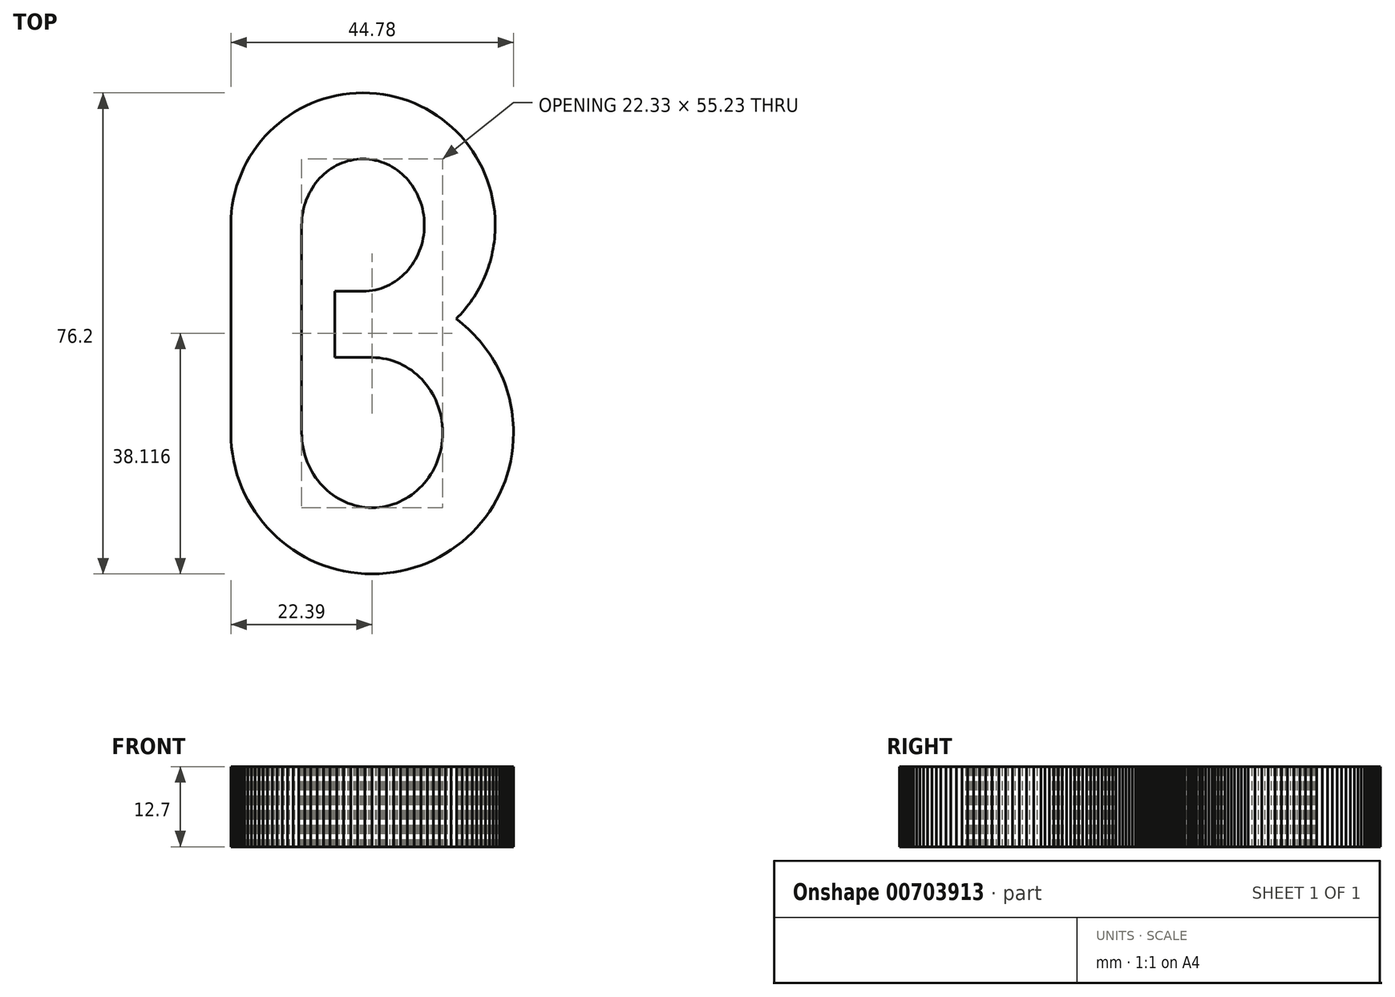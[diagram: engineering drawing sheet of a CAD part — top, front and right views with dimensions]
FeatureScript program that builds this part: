
annotation { "Feature Type Name" : "Feature", "Feature Type Description" : "" }
export const myFeature = defineFeature(function(context is Context, id is Id, definition is map)
    precondition{}
    {
        {
            var Q0;
            Q0=qCreatedBy(makeId("Top.planeOp"),FACE);
            var sketch = newSketch(context, id + "F0", { "sketchPlane" : qUnion([Q0])});
            skLineSegment(sketch, "E0", {"start": v(13.3, 2.3) * mm, "end": v(13.66, 2.66) * mm});
            skLineSegment(sketch, "E1", {"start": v(13.66, 2.66) * mm, "end": v(14, 3.03) * mm});
            skLineSegment(sketch, "E2", {"start": v(14, 3.03) * mm, "end": v(14.34, 3.4) * mm});
            skLineSegment(sketch, "E3", {"start": v(14.34, 3.4) * mm, "end": v(14.67, 3.8) * mm});
            skLineSegment(sketch, "E4", {"start": v(14.67, 3.8) * mm, "end": v(14.99, 4.18) * mm});
            skLineSegment(sketch, "E5", {"start": v(14.99, 4.18) * mm, "end": v(15.3, 4.58) * mm});
            skLineSegment(sketch, "E6", {"start": v(15.3, 4.58) * mm, "end": v(15.6, 5) * mm});
            skLineSegment(sketch, "E7", {"start": v(15.6, 5) * mm, "end": v(15.89, 5.4) * mm});
            skLineSegment(sketch, "E8", {"start": v(15.89, 5.4) * mm, "end": v(16.16, 5.83) * mm});
            skLineSegment(sketch, "E9", {"start": v(16.16, 5.83) * mm, "end": v(16.43, 6.26) * mm});
            skLineSegment(sketch, "E10", {"start": v(16.43, 6.26) * mm, "end": v(16.7, 6.7) * mm});
            skLineSegment(sketch, "E11", {"start": v(16.7, 6.7) * mm, "end": v(16.94, 7.14) * mm});
            skLineSegment(sketch, "E12", {"start": v(16.94, 7.14) * mm, "end": v(17.18, 7.59) * mm});
            skLineSegment(sketch, "E13", {"start": v(17.18, 7.59) * mm, "end": v(17.4, 8.04) * mm});
            skLineSegment(sketch, "E14", {"start": v(17.4, 8.04) * mm, "end": v(17.63, 8.5) * mm});
            skLineSegment(sketch, "E15", {"start": v(17.63, 8.5) * mm, "end": v(17.83, 8.97) * mm});
            skLineSegment(sketch, "E16", {"start": v(17.83, 8.97) * mm, "end": v(18.03, 9.45) * mm});
            skLineSegment(sketch, "E17", {"start": v(18.03, 9.45) * mm, "end": v(18.2, 9.93) * mm});
            skLineSegment(sketch, "E18", {"start": v(18.2, 9.93) * mm, "end": v(18.38, 10.41) * mm});
            skLineSegment(sketch, "E19", {"start": v(18.38, 10.41) * mm, "end": v(18.54, 10.9) * mm});
            skLineSegment(sketch, "E20", {"start": v(18.54, 10.9) * mm, "end": v(18.7, 11.4) * mm});
            skLineSegment(sketch, "E21", {"start": v(18.7, 11.4) * mm, "end": v(18.83, 11.9) * mm});
            skLineSegment(sketch, "E22", {"start": v(18.83, 11.9) * mm, "end": v(18.95, 12.4) * mm});
            skLineSegment(sketch, "E23", {"start": v(18.95, 12.4) * mm, "end": v(19.06, 12.92) * mm});
            skLineSegment(sketch, "E24", {"start": v(19.06, 12.92) * mm, "end": v(19.16, 13.44) * mm});
            skLineSegment(sketch, "E25", {"start": v(19.16, 13.44) * mm, "end": v(19.25, 13.96) * mm});
            skLineSegment(sketch, "E26", {"start": v(19.25, 13.96) * mm, "end": v(19.32, 14.48) * mm});
            skLineSegment(sketch, "E27", {"start": v(19.32, 14.48) * mm, "end": v(19.38, 15) * mm});
            skLineSegment(sketch, "E28", {"start": v(19.38, 15) * mm, "end": v(19.43, 15.54) * mm});
            skLineSegment(sketch, "E29", {"start": v(19.43, 15.54) * mm, "end": v(19.46, 16.08) * mm});
            skLineSegment(sketch, "E30", {"start": v(19.46, 16.08) * mm, "end": v(19.48, 16.61) * mm});
            skLineSegment(sketch, "E31", {"start": v(19.48, 16.61) * mm, "end": v(19.5, 17.16) * mm});
            skLineSegment(sketch, "E32", {"start": v(19.5, 17.16) * mm, "end": v(19.46, 18.24) * mm});
            skLineSegment(sketch, "E33", {"start": v(19.46, 18.24) * mm, "end": v(19.38, 19.3) * mm});
            skLineSegment(sketch, "E34", {"start": v(19.38, 19.3) * mm, "end": v(19.25, 20.35) * mm});
            skLineSegment(sketch, "E35", {"start": v(19.25, 20.35) * mm, "end": v(19.07, 21.38) * mm});
            skLineSegment(sketch, "E36", {"start": v(19.07, 21.38) * mm, "end": v(18.83, 22.4) * mm});
            skLineSegment(sketch, "E37", {"start": v(18.83, 22.4) * mm, "end": v(18.55, 23.39) * mm});
            skLineSegment(sketch, "E38", {"start": v(18.55, 23.39) * mm, "end": v(18.22, 24.36) * mm});
            skLineSegment(sketch, "E39", {"start": v(18.22, 24.36) * mm, "end": v(17.85, 25.3) * mm});
            skLineSegment(sketch, "E40", {"start": v(17.85, 25.3) * mm, "end": v(17.43, 26.24) * mm});
            skLineSegment(sketch, "E41", {"start": v(17.43, 26.24) * mm, "end": v(16.96, 27.14) * mm});
            skLineSegment(sketch, "E42", {"start": v(16.96, 27.14) * mm, "end": v(16.46, 28.02) * mm});
            skLineSegment(sketch, "E43", {"start": v(16.46, 28.02) * mm, "end": v(15.91, 28.87) * mm});
            skLineSegment(sketch, "E44", {"start": v(15.91, 28.87) * mm, "end": v(15.33, 29.69) * mm});
            skLineSegment(sketch, "E45", {"start": v(15.33, 29.69) * mm, "end": v(14.7, 30.48) * mm});
            skLineSegment(sketch, "E46", {"start": v(14.7, 30.48) * mm, "end": v(14.05, 31.24) * mm});
            skLineSegment(sketch, "E47", {"start": v(14.05, 31.24) * mm, "end": v(13.36, 31.97) * mm});
            skLineSegment(sketch, "E48", {"start": v(13.36, 31.97) * mm, "end": v(12.63, 32.66) * mm});
            skLineSegment(sketch, "E49", {"start": v(12.63, 32.66) * mm, "end": v(11.87, 33.32) * mm});
            skLineSegment(sketch, "E50", {"start": v(11.87, 33.32) * mm, "end": v(11.08, 33.94) * mm});
            skLineSegment(sketch, "E51", {"start": v(11.08, 33.94) * mm, "end": v(10.26, 34.52) * mm});
            skLineSegment(sketch, "E52", {"start": v(10.26, 34.52) * mm, "end": v(9.4, 35.07) * mm});
            skLineSegment(sketch, "E53", {"start": v(9.4, 35.07) * mm, "end": v(8.53, 35.57) * mm});
            skLineSegment(sketch, "E54", {"start": v(8.53, 35.57) * mm, "end": v(7.63, 36.03) * mm});
            skLineSegment(sketch, "E55", {"start": v(7.63, 36.03) * mm, "end": v(6.7, 36.45) * mm});
            skLineSegment(sketch, "E56", {"start": v(6.7, 36.45) * mm, "end": v(5.75, 36.83) * mm});
            skLineSegment(sketch, "E57", {"start": v(5.75, 36.83) * mm, "end": v(4.78, 37.16) * mm});
            skLineSegment(sketch, "E58", {"start": v(4.78, 37.16) * mm, "end": v(3.78, 37.44) * mm});
            skLineSegment(sketch, "E59", {"start": v(3.78, 37.44) * mm, "end": v(2.77, 37.67) * mm});
            skLineSegment(sketch, "E60", {"start": v(2.77, 37.67) * mm, "end": v(1.74, 37.86) * mm});
            skLineSegment(sketch, "E61", {"start": v(1.74, 37.86) * mm, "end": v(0.7, 38) * mm});
            skLineSegment(sketch, "E62", {"start": v(0.7, 38) * mm, "end": v(-0.37, 38.07) * mm});
            skLineSegment(sketch, "E63", {"start": v(-0.37, 38.07) * mm, "end": v(-1.45, 38.1) * mm});
            skLineSegment(sketch, "E64", {"start": v(-1.45, 38.1) * mm, "end": v(-2.53, 38.07) * mm});
            skLineSegment(sketch, "E65", {"start": v(-2.53, 38.07) * mm, "end": v(-3.6, 38) * mm});
            skLineSegment(sketch, "E66", {"start": v(-3.6, 38) * mm, "end": v(-4.64, 37.86) * mm});
            skLineSegment(sketch, "E67", {"start": v(-4.64, 37.86) * mm, "end": v(-5.67, 37.67) * mm});
            skLineSegment(sketch, "E68", {"start": v(-5.67, 37.67) * mm, "end": v(-6.68, 37.44) * mm});
            skLineSegment(sketch, "E69", {"start": v(-6.68, 37.44) * mm, "end": v(-7.68, 37.16) * mm});
            skLineSegment(sketch, "E70", {"start": v(-7.68, 37.16) * mm, "end": v(-8.65, 36.83) * mm});
            skLineSegment(sketch, "E71", {"start": v(-8.65, 36.83) * mm, "end": v(-9.6, 36.45) * mm});
            skLineSegment(sketch, "E72", {"start": v(-9.6, 36.45) * mm, "end": v(-10.53, 36.03) * mm});
            skLineSegment(sketch, "E73", {"start": v(-10.53, 36.03) * mm, "end": v(-11.43, 35.57) * mm});
            skLineSegment(sketch, "E74", {"start": v(-11.43, 35.57) * mm, "end": v(-12.31, 35.07) * mm});
            skLineSegment(sketch, "E75", {"start": v(-12.31, 35.07) * mm, "end": v(-13.16, 34.52) * mm});
            skLineSegment(sketch, "E76", {"start": v(-13.16, 34.52) * mm, "end": v(-13.98, 33.94) * mm});
            skLineSegment(sketch, "E77", {"start": v(-13.98, 33.94) * mm, "end": v(-14.77, 33.32) * mm});
            skLineSegment(sketch, "E78", {"start": v(-14.77, 33.32) * mm, "end": v(-15.53, 32.66) * mm});
            skLineSegment(sketch, "E79", {"start": v(-15.53, 32.66) * mm, "end": v(-16.26, 31.97) * mm});
            skLineSegment(sketch, "E80", {"start": v(-16.26, 31.97) * mm, "end": v(-16.95, 31.24) * mm});
            skLineSegment(sketch, "E81", {"start": v(-16.95, 31.24) * mm, "end": v(-17.61, 30.48) * mm});
            skLineSegment(sketch, "E82", {"start": v(-17.61, 30.48) * mm, "end": v(-18.23, 29.69) * mm});
            skLineSegment(sketch, "E83", {"start": v(-18.23, 29.69) * mm, "end": v(-18.82, 28.87) * mm});
            skLineSegment(sketch, "E84", {"start": v(-18.82, 28.87) * mm, "end": v(-19.36, 28.02) * mm});
            skLineSegment(sketch, "E85", {"start": v(-19.36, 28.02) * mm, "end": v(-19.87, 27.14) * mm});
            skLineSegment(sketch, "E86", {"start": v(-19.87, 27.14) * mm, "end": v(-20.33, 26.24) * mm});
            skLineSegment(sketch, "E87", {"start": v(-20.33, 26.24) * mm, "end": v(-20.75, 25.3) * mm});
            skLineSegment(sketch, "E88", {"start": v(-20.75, 25.3) * mm, "end": v(-21.12, 24.36) * mm});
            skLineSegment(sketch, "E89", {"start": v(-21.12, 24.36) * mm, "end": v(-21.45, 23.39) * mm});
            skLineSegment(sketch, "E90", {"start": v(-21.45, 23.39) * mm, "end": v(-21.73, 22.4) * mm});
            skLineSegment(sketch, "E91", {"start": v(-21.73, 22.4) * mm, "end": v(-21.97, 21.38) * mm});
            skLineSegment(sketch, "E92", {"start": v(-21.97, 21.38) * mm, "end": v(-22.15, 20.35) * mm});
            skLineSegment(sketch, "E93", {"start": v(-22.15, 20.35) * mm, "end": v(-22.29, 19.3) * mm});
            skLineSegment(sketch, "E94", {"start": v(-22.29, 19.3) * mm, "end": v(-22.37, 18.24) * mm});
            skLineSegment(sketch, "E95", {"start": v(-22.37, 18.24) * mm, "end": v(-22.4, 17.16) * mm});
            skLineSegment(sketch, "E96", {"start": v(-22.4, 17.16) * mm, "end": v(-22.4, 16.51) * mm});
            skLineSegment(sketch, "E97", {"start": v(-22.4, 16.51) * mm, "end": v(-22.4, 15.8) * mm});
            skLineSegment(sketch, "E98", {"start": v(-22.4, 15.8) * mm, "end": v(-22.4, 15) * mm});
            skLineSegment(sketch, "E99", {"start": v(-22.4, 15) * mm, "end": v(-22.4, 14.16) * mm});
            skLineSegment(sketch, "E100", {"start": v(-22.4, 14.16) * mm, "end": v(-22.4, 13.25) * mm});
            skLineSegment(sketch, "E101", {"start": v(-22.4, 13.25) * mm, "end": v(-22.4, 12.3) * mm});
            skLineSegment(sketch, "E102", {"start": v(-22.4, 12.3) * mm, "end": v(-22.4, 11.28) * mm});
            skLineSegment(sketch, "E103", {"start": v(-22.4, 11.28) * mm, "end": v(-22.4, 10.23) * mm});
            skLineSegment(sketch, "E104", {"start": v(-22.4, 10.23) * mm, "end": v(-22.4, 9.14) * mm});
            skLineSegment(sketch, "E105", {"start": v(-22.4, 9.14) * mm, "end": v(-22.4, 8.01) * mm});
            skLineSegment(sketch, "E106", {"start": v(-22.4, 8.01) * mm, "end": v(-22.4, 6.85) * mm});
            skLineSegment(sketch, "E107", {"start": v(-22.4, 6.85) * mm, "end": v(-22.4, 5.67) * mm});
            skLineSegment(sketch, "E108", {"start": v(-22.4, 5.67) * mm, "end": v(-22.4, 4.47) * mm});
            skLineSegment(sketch, "E109", {"start": v(-22.4, 4.47) * mm, "end": v(-22.4, 3.26) * mm});
            skLineSegment(sketch, "E110", {"start": v(-22.4, 3.26) * mm, "end": v(-22.4, 2.03) * mm});
            skLineSegment(sketch, "E111", {"start": v(-22.4, 2.03) * mm, "end": v(-22.4, 0.8) * mm});
            skLineSegment(sketch, "E112", {"start": v(-22.4, 0.8) * mm, "end": v(-22.4, -0.43) * mm});
            skLineSegment(sketch, "E113", {"start": v(-22.4, -0.43) * mm, "end": v(-22.4, -1.66) * mm});
            skLineSegment(sketch, "E114", {"start": v(-22.4, -1.66) * mm, "end": v(-22.4, -2.88) * mm});
            skLineSegment(sketch, "E115", {"start": v(-22.4, -2.88) * mm, "end": v(-22.4, -4.08) * mm});
            skLineSegment(sketch, "E116", {"start": v(-22.4, -4.08) * mm, "end": v(-22.4, -5.27) * mm});
            skLineSegment(sketch, "E117", {"start": v(-22.4, -5.27) * mm, "end": v(-22.4, -6.43) * mm});
            skLineSegment(sketch, "E118", {"start": v(-22.4, -6.43) * mm, "end": v(-22.4, -7.57) * mm});
            skLineSegment(sketch, "E119", {"start": v(-22.4, -7.57) * mm, "end": v(-22.4, -8.67) * mm});
            skLineSegment(sketch, "E120", {"start": v(-22.4, -8.67) * mm, "end": v(-22.4, -9.73) * mm});
            skLineSegment(sketch, "E121", {"start": v(-22.4, -9.73) * mm, "end": v(-22.4, -10.75) * mm});
            skLineSegment(sketch, "E122", {"start": v(-22.4, -10.75) * mm, "end": v(-22.4, -11.72) * mm});
            skLineSegment(sketch, "E123", {"start": v(-22.4, -11.72) * mm, "end": v(-22.4, -12.64) * mm});
            skLineSegment(sketch, "E124", {"start": v(-22.4, -12.64) * mm, "end": v(-22.4, -13.5) * mm});
            skLineSegment(sketch, "E125", {"start": v(-22.4, -13.5) * mm, "end": v(-22.4, -14.3) * mm});
            skLineSegment(sketch, "E126", {"start": v(-22.4, -14.3) * mm, "end": v(-22.4, -15.04) * mm});
            skLineSegment(sketch, "E127", {"start": v(-22.4, -15.04) * mm, "end": v(-22.4, -15.7) * mm});
            skLineSegment(sketch, "E128", {"start": v(-22.4, -15.7) * mm, "end": v(-22.36, -16.86) * mm});
            skLineSegment(sketch, "E129", {"start": v(-22.36, -16.86) * mm, "end": v(-22.28, -18) * mm});
            skLineSegment(sketch, "E130", {"start": v(-22.28, -18) * mm, "end": v(-22.14, -19.12) * mm});
            skLineSegment(sketch, "E131", {"start": v(-22.14, -19.12) * mm, "end": v(-21.94, -20.22) * mm});
            skLineSegment(sketch, "E132", {"start": v(-21.94, -20.22) * mm, "end": v(-21.69, -21.3) * mm});
            skLineSegment(sketch, "E133", {"start": v(-21.69, -21.3) * mm, "end": v(-21.39, -22.37) * mm});
            skLineSegment(sketch, "E134", {"start": v(-21.39, -22.37) * mm, "end": v(-21.03, -23.4) * mm});
            skLineSegment(sketch, "E135", {"start": v(-21.03, -23.4) * mm, "end": v(-20.63, -24.42) * mm});
            skLineSegment(sketch, "E136", {"start": v(-20.63, -24.42) * mm, "end": v(-20.18, -25.42) * mm});
            skLineSegment(sketch, "E137", {"start": v(-20.18, -25.42) * mm, "end": v(-19.7, -26.38) * mm});
            skLineSegment(sketch, "E138", {"start": v(-19.7, -26.38) * mm, "end": v(-19.15, -27.32) * mm});
            skLineSegment(sketch, "E139", {"start": v(-19.15, -27.32) * mm, "end": v(-18.57, -28.23) * mm});
            skLineSegment(sketch, "E140", {"start": v(-18.57, -28.23) * mm, "end": v(-17.94, -29.1) * mm});
            skLineSegment(sketch, "E141", {"start": v(-17.94, -29.1) * mm, "end": v(-17.28, -29.95) * mm});
            skLineSegment(sketch, "E142", {"start": v(-17.28, -29.95) * mm, "end": v(-16.58, -30.76) * mm});
            skLineSegment(sketch, "E143", {"start": v(-16.58, -30.76) * mm, "end": v(-15.83, -31.54) * mm});
            skLineSegment(sketch, "E144", {"start": v(-15.83, -31.54) * mm, "end": v(-15.06, -32.28) * mm});
            skLineSegment(sketch, "E145", {"start": v(-15.06, -32.28) * mm, "end": v(-14.24, -32.99) * mm});
            skLineSegment(sketch, "E146", {"start": v(-14.24, -32.99) * mm, "end": v(-13.4, -33.65) * mm});
            skLineSegment(sketch, "E147", {"start": v(-13.4, -33.65) * mm, "end": v(-12.52, -34.28) * mm});
            skLineSegment(sketch, "E148", {"start": v(-12.52, -34.28) * mm, "end": v(-11.61, -34.86) * mm});
            skLineSegment(sketch, "E149", {"start": v(-11.61, -34.86) * mm, "end": v(-10.67, -35.4) * mm});
            skLineSegment(sketch, "E150", {"start": v(-10.67, -35.4) * mm, "end": v(-9.7, -35.9) * mm});
            skLineSegment(sketch, "E151", {"start": v(-9.7, -35.9) * mm, "end": v(-8.72, -36.34) * mm});
            skLineSegment(sketch, "E152", {"start": v(-8.72, -36.34) * mm, "end": v(-7.7, -36.74) * mm});
            skLineSegment(sketch, "E153", {"start": v(-7.7, -36.74) * mm, "end": v(-6.66, -37.1) * mm});
            skLineSegment(sketch, "E154", {"start": v(-6.66, -37.1) * mm, "end": v(-5.6, -37.4) * mm});
            skLineSegment(sketch, "E155", {"start": v(-5.6, -37.4) * mm, "end": v(-4.51, -37.65) * mm});
            skLineSegment(sketch, "E156", {"start": v(-4.51, -37.65) * mm, "end": v(-3.41, -37.84) * mm});
            skLineSegment(sketch, "E157", {"start": v(-3.41, -37.84) * mm, "end": v(-2.29, -37.98) * mm});
            skLineSegment(sketch, "E158", {"start": v(-2.29, -37.98) * mm, "end": v(-1.15, -38.07) * mm});
            skLineSegment(sketch, "E159", {"start": v(-1.15, -38.07) * mm, "end": v(0, -38.1) * mm});
            skLineSegment(sketch, "E160", {"start": v(0, -38.1) * mm, "end": v(1.15, -38.07) * mm});
            skLineSegment(sketch, "E161", {"start": v(1.15, -38.07) * mm, "end": v(2.29, -37.98) * mm});
            skLineSegment(sketch, "E162", {"start": v(2.29, -37.98) * mm, "end": v(3.41, -37.84) * mm});
            skLineSegment(sketch, "E163", {"start": v(3.41, -37.84) * mm, "end": v(4.51, -37.65) * mm});
            skLineSegment(sketch, "E164", {"start": v(4.51, -37.65) * mm, "end": v(5.6, -37.4) * mm});
            skLineSegment(sketch, "E165", {"start": v(5.6, -37.4) * mm, "end": v(6.66, -37.1) * mm});
            skLineSegment(sketch, "E166", {"start": v(6.66, -37.1) * mm, "end": v(7.7, -36.74) * mm});
            skLineSegment(sketch, "E167", {"start": v(7.7, -36.74) * mm, "end": v(8.72, -36.34) * mm});
            skLineSegment(sketch, "E168", {"start": v(8.72, -36.34) * mm, "end": v(9.7, -35.9) * mm});
            skLineSegment(sketch, "E169", {"start": v(9.7, -35.9) * mm, "end": v(10.67, -35.4) * mm});
            skLineSegment(sketch, "E170", {"start": v(10.67, -35.4) * mm, "end": v(11.61, -34.86) * mm});
            skLineSegment(sketch, "E171", {"start": v(11.61, -34.86) * mm, "end": v(12.52, -34.28) * mm});
            skLineSegment(sketch, "E172", {"start": v(12.52, -34.28) * mm, "end": v(13.4, -33.65) * mm});
            skLineSegment(sketch, "E173", {"start": v(13.4, -33.65) * mm, "end": v(14.24, -32.99) * mm});
            skLineSegment(sketch, "E174", {"start": v(14.24, -32.99) * mm, "end": v(15.06, -32.28) * mm});
            skLineSegment(sketch, "E175", {"start": v(15.06, -32.28) * mm, "end": v(15.83, -31.54) * mm});
            skLineSegment(sketch, "E176", {"start": v(15.83, -31.54) * mm, "end": v(16.58, -30.76) * mm});
            skLineSegment(sketch, "E177", {"start": v(16.58, -30.76) * mm, "end": v(17.28, -29.95) * mm});
            skLineSegment(sketch, "E178", {"start": v(17.28, -29.95) * mm, "end": v(17.94, -29.1) * mm});
            skLineSegment(sketch, "E179", {"start": v(17.94, -29.1) * mm, "end": v(18.57, -28.23) * mm});
            skLineSegment(sketch, "E180", {"start": v(18.57, -28.23) * mm, "end": v(19.15, -27.32) * mm});
            skLineSegment(sketch, "E181", {"start": v(19.15, -27.32) * mm, "end": v(19.7, -26.38) * mm});
            skLineSegment(sketch, "E182", {"start": v(19.7, -26.38) * mm, "end": v(20.18, -25.42) * mm});
            skLineSegment(sketch, "E183", {"start": v(20.18, -25.42) * mm, "end": v(20.63, -24.42) * mm});
            skLineSegment(sketch, "E184", {"start": v(20.63, -24.42) * mm, "end": v(21.03, -23.4) * mm});
            skLineSegment(sketch, "E185", {"start": v(21.03, -23.4) * mm, "end": v(21.39, -22.37) * mm});
            skLineSegment(sketch, "E186", {"start": v(21.39, -22.37) * mm, "end": v(21.69, -21.3) * mm});
            skLineSegment(sketch, "E187", {"start": v(21.69, -21.3) * mm, "end": v(21.94, -20.22) * mm});
            skLineSegment(sketch, "E188", {"start": v(21.94, -20.22) * mm, "end": v(22.14, -19.12) * mm});
            skLineSegment(sketch, "E189", {"start": v(22.14, -19.12) * mm, "end": v(22.28, -18) * mm});
            skLineSegment(sketch, "E190", {"start": v(22.28, -18) * mm, "end": v(22.36, -16.86) * mm});
            skLineSegment(sketch, "E191", {"start": v(22.36, -16.86) * mm, "end": v(22.4, -15.7) * mm});
            skLineSegment(sketch, "E192", {"start": v(22.4, -15.7) * mm, "end": v(22.38, -15.02) * mm});
            skLineSegment(sketch, "E193", {"start": v(22.38, -15.02) * mm, "end": v(22.35, -14.33) * mm});
            skLineSegment(sketch, "E194", {"start": v(22.35, -14.33) * mm, "end": v(22.3, -13.65) * mm});
            skLineSegment(sketch, "E195", {"start": v(22.3, -13.65) * mm, "end": v(22.23, -12.98) * mm});
            skLineSegment(sketch, "E196", {"start": v(22.23, -12.98) * mm, "end": v(22.14, -12.31) * mm});
            skLineSegment(sketch, "E197", {"start": v(22.14, -12.31) * mm, "end": v(22.03, -11.65) * mm});
            skLineSegment(sketch, "E198", {"start": v(22.03, -11.65) * mm, "end": v(21.9, -11) * mm});
            skLineSegment(sketch, "E199", {"start": v(21.9, -11) * mm, "end": v(21.75, -10.35) * mm});
            skLineSegment(sketch, "E200", {"start": v(21.75, -10.35) * mm, "end": v(21.58, -9.71) * mm});
            skLineSegment(sketch, "E201", {"start": v(21.58, -9.71) * mm, "end": v(21.4, -9.08) * mm});
            skLineSegment(sketch, "E202", {"start": v(21.4, -9.08) * mm, "end": v(21.2, -8.46) * mm});
            skLineSegment(sketch, "E203", {"start": v(21.2, -8.46) * mm, "end": v(20.97, -7.84) * mm});
            skLineSegment(sketch, "E204", {"start": v(20.97, -7.84) * mm, "end": v(20.73, -7.23) * mm});
            skLineSegment(sketch, "E205", {"start": v(20.73, -7.23) * mm, "end": v(20.48, -6.63) * mm});
            skLineSegment(sketch, "E206", {"start": v(20.48, -6.63) * mm, "end": v(20.2, -6.04) * mm});
            skLineSegment(sketch, "E207", {"start": v(20.2, -6.04) * mm, "end": v(19.92, -5.46) * mm});
            skLineSegment(sketch, "E208", {"start": v(19.92, -5.46) * mm, "end": v(19.61, -4.9) * mm});
            skLineSegment(sketch, "E209", {"start": v(19.61, -4.9) * mm, "end": v(19.3, -4.33) * mm});
            skLineSegment(sketch, "E210", {"start": v(19.3, -4.33) * mm, "end": v(18.96, -3.78) * mm});
            skLineSegment(sketch, "E211", {"start": v(18.96, -3.78) * mm, "end": v(18.6, -3.24) * mm});
            skLineSegment(sketch, "E212", {"start": v(18.6, -3.24) * mm, "end": v(18.24, -2.71) * mm});
            skLineSegment(sketch, "E213", {"start": v(18.24, -2.71) * mm, "end": v(17.86, -2.2) * mm});
            skLineSegment(sketch, "E214", {"start": v(17.86, -2.2) * mm, "end": v(17.46, -1.69) * mm});
            skLineSegment(sketch, "E215", {"start": v(17.46, -1.69) * mm, "end": v(17.05, -1.2) * mm});
            skLineSegment(sketch, "E216", {"start": v(17.05, -1.2) * mm, "end": v(16.63, -0.71) * mm});
            skLineSegment(sketch, "E217", {"start": v(16.63, -0.71) * mm, "end": v(16.2, -0.24) * mm});
            skLineSegment(sketch, "E218", {"start": v(16.2, -0.24) * mm, "end": v(15.74, 0.22) * mm});
            skLineSegment(sketch, "E219", {"start": v(15.74, 0.22) * mm, "end": v(15.28, 0.66) * mm});
            skLineSegment(sketch, "E220", {"start": v(15.28, 0.66) * mm, "end": v(14.8, 1.1) * mm});
            skLineSegment(sketch, "E221", {"start": v(14.8, 1.1) * mm, "end": v(14.32, 1.5) * mm});
            skLineSegment(sketch, "E222", {"start": v(14.32, 1.5) * mm, "end": v(13.82, 1.91) * mm});
            skLineSegment(sketch, "E223", {"start": v(13.82, 1.91) * mm, "end": v(13.3, 2.3) * mm});
            skLineSegment(sketch, "E224", {"start": v(0, -27.6) * mm, "end": v(-0.57, -27.58) * mm});
            skLineSegment(sketch, "E225", {"start": v(-0.57, -27.58) * mm, "end": v(-1.14, -27.54) * mm});
            skLineSegment(sketch, "E226", {"start": v(-1.14, -27.54) * mm, "end": v(-1.7, -27.46) * mm});
            skLineSegment(sketch, "E227", {"start": v(-1.7, -27.46) * mm, "end": v(-2.25, -27.36) * mm});
            skLineSegment(sketch, "E228", {"start": v(-2.25, -27.36) * mm, "end": v(-2.8, -27.22) * mm});
            skLineSegment(sketch, "E229", {"start": v(-2.8, -27.22) * mm, "end": v(-3.32, -27.06) * mm});
            skLineSegment(sketch, "E230", {"start": v(-3.32, -27.06) * mm, "end": v(-3.84, -26.88) * mm});
            skLineSegment(sketch, "E231", {"start": v(-3.84, -26.88) * mm, "end": v(-4.35, -26.66) * mm});
            skLineSegment(sketch, "E232", {"start": v(-4.35, -26.66) * mm, "end": v(-4.84, -26.42) * mm});
            skLineSegment(sketch, "E233", {"start": v(-4.84, -26.42) * mm, "end": v(-5.32, -26.16) * mm});
            skLineSegment(sketch, "E234", {"start": v(-5.32, -26.16) * mm, "end": v(-5.79, -25.88) * mm});
            skLineSegment(sketch, "E235", {"start": v(-5.79, -25.88) * mm, "end": v(-6.24, -25.57) * mm});
            skLineSegment(sketch, "E236", {"start": v(-6.24, -25.57) * mm, "end": v(-6.68, -25.24) * mm});
            skLineSegment(sketch, "E237", {"start": v(-6.68, -25.24) * mm, "end": v(-7.1, -24.88) * mm});
            skLineSegment(sketch, "E238", {"start": v(-7.1, -24.88) * mm, "end": v(-7.5, -24.5) * mm});
            skLineSegment(sketch, "E239", {"start": v(-7.5, -24.5) * mm, "end": v(-7.9, -24.11) * mm});
            skLineSegment(sketch, "E240", {"start": v(-7.9, -24.11) * mm, "end": v(-8.26, -23.7) * mm});
            skLineSegment(sketch, "E241", {"start": v(-8.26, -23.7) * mm, "end": v(-8.62, -23.27) * mm});
            skLineSegment(sketch, "E242", {"start": v(-8.62, -23.27) * mm, "end": v(-8.95, -22.82) * mm});
            skLineSegment(sketch, "E243", {"start": v(-8.95, -22.82) * mm, "end": v(-9.26, -22.35) * mm});
            skLineSegment(sketch, "E244", {"start": v(-9.26, -22.35) * mm, "end": v(-9.55, -21.87) * mm});
            skLineSegment(sketch, "E245", {"start": v(-9.55, -21.87) * mm, "end": v(-9.82, -21.37) * mm});
            skLineSegment(sketch, "E246", {"start": v(-9.82, -21.37) * mm, "end": v(-10.06, -20.86) * mm});
            skLineSegment(sketch, "E247", {"start": v(-10.06, -20.86) * mm, "end": v(-10.29, -20.34) * mm});
            skLineSegment(sketch, "E248", {"start": v(-10.29, -20.34) * mm, "end": v(-10.49, -19.8) * mm});
            skLineSegment(sketch, "E249", {"start": v(-10.49, -19.8) * mm, "end": v(-10.66, -19.24) * mm});
            skLineSegment(sketch, "E250", {"start": v(-10.66, -19.24) * mm, "end": v(-10.81, -18.68) * mm});
            skLineSegment(sketch, "E251", {"start": v(-10.81, -18.68) * mm, "end": v(-10.94, -18.1) * mm});
            skLineSegment(sketch, "E252", {"start": v(-10.94, -18.1) * mm, "end": v(-11.04, -17.52) * mm});
            skLineSegment(sketch, "E253", {"start": v(-11.04, -17.52) * mm, "end": v(-11.1, -16.92) * mm});
            skLineSegment(sketch, "E254", {"start": v(-11.1, -16.92) * mm, "end": v(-11.15, -16.32) * mm});
            skLineSegment(sketch, "E255", {"start": v(-11.15, -16.32) * mm, "end": v(-11.17, -15.7) * mm});
            skLineSegment(sketch, "E256", {"start": v(-11.17, -15.7) * mm, "end": v(-11.17, -15.42) * mm});
            skLineSegment(sketch, "E257", {"start": v(-11.17, -15.42) * mm, "end": v(-11.17, -14.99) * mm});
            skLineSegment(sketch, "E258", {"start": v(-11.17, -14.99) * mm, "end": v(-11.17, -14.43) * mm});
            skLineSegment(sketch, "E259", {"start": v(-11.17, -14.43) * mm, "end": v(-11.17, -13.75) * mm});
            skLineSegment(sketch, "E260", {"start": v(-11.17, -13.75) * mm, "end": v(-11.17, -12.95) * mm});
            skLineSegment(sketch, "E261", {"start": v(-11.17, -12.95) * mm, "end": v(-11.17, -12.05) * mm});
            skLineSegment(sketch, "E262", {"start": v(-11.17, -12.05) * mm, "end": v(-11.17, -11.06) * mm});
            skLineSegment(sketch, "E263", {"start": v(-11.17, -11.06) * mm, "end": v(-11.17, -9.99) * mm});
            skLineSegment(sketch, "E264", {"start": v(-11.17, -9.99) * mm, "end": v(-11.17, -8.84) * mm});
            skLineSegment(sketch, "E265", {"start": v(-11.17, -8.84) * mm, "end": v(-11.17, -7.62) * mm});
            skLineSegment(sketch, "E266", {"start": v(-11.17, -7.62) * mm, "end": v(-11.17, -6.35) * mm});
            skLineSegment(sketch, "E267", {"start": v(-11.17, -6.35) * mm, "end": v(-11.17, -5.03) * mm});
            skLineSegment(sketch, "E268", {"start": v(-11.17, -5.03) * mm, "end": v(-11.17, -3.67) * mm});
            skLineSegment(sketch, "E269", {"start": v(-11.17, -3.67) * mm, "end": v(-11.17, -2.29) * mm});
            skLineSegment(sketch, "E270", {"start": v(-11.17, -2.29) * mm, "end": v(-11.17, -0.88) * mm});
            skLineSegment(sketch, "E271", {"start": v(-11.17, -0.88) * mm, "end": v(-11.17, 0.54) * mm});
            skLineSegment(sketch, "E272", {"start": v(-11.17, 0.54) * mm, "end": v(-11.17, 1.96) * mm});
            skLineSegment(sketch, "E273", {"start": v(-11.17, 1.96) * mm, "end": v(-11.17, 3.37) * mm});
            skLineSegment(sketch, "E274", {"start": v(-11.17, 3.37) * mm, "end": v(-11.17, 4.77) * mm});
            skLineSegment(sketch, "E275", {"start": v(-11.17, 4.77) * mm, "end": v(-11.17, 6.14) * mm});
            skLineSegment(sketch, "E276", {"start": v(-11.17, 6.14) * mm, "end": v(-11.17, 7.47) * mm});
            skLineSegment(sketch, "E277", {"start": v(-11.17, 7.47) * mm, "end": v(-11.17, 8.76) * mm});
            skLineSegment(sketch, "E278", {"start": v(-11.17, 8.76) * mm, "end": v(-11.17, 10) * mm});
            skLineSegment(sketch, "E279", {"start": v(-11.17, 10) * mm, "end": v(-11.17, 11.16) * mm});
            skLineSegment(sketch, "E280", {"start": v(-11.17, 11.16) * mm, "end": v(-11.17, 12.26) * mm});
            skLineSegment(sketch, "E281", {"start": v(-11.17, 12.26) * mm, "end": v(-11.17, 13.28) * mm});
            skLineSegment(sketch, "E282", {"start": v(-11.17, 13.28) * mm, "end": v(-11.17, 14.2) * mm});
            skLineSegment(sketch, "E283", {"start": v(-11.17, 14.2) * mm, "end": v(-11.17, 15.03) * mm});
            skLineSegment(sketch, "E284", {"start": v(-11.17, 15.03) * mm, "end": v(-11.17, 15.75) * mm});
            skLineSegment(sketch, "E285", {"start": v(-11.17, 15.75) * mm, "end": v(-11.17, 16.35) * mm});
            skLineSegment(sketch, "E286", {"start": v(-11.17, 16.35) * mm, "end": v(-11.17, 16.82) * mm});
            skLineSegment(sketch, "E287", {"start": v(-11.17, 16.82) * mm, "end": v(-11.17, 17.16) * mm});
            skLineSegment(sketch, "E288", {"start": v(-11.17, 17.16) * mm, "end": v(-11.15, 17.7) * mm});
            skLineSegment(sketch, "E289", {"start": v(-11.15, 17.7) * mm, "end": v(-11.11, 18.23) * mm});
            skLineSegment(sketch, "E290", {"start": v(-11.11, 18.23) * mm, "end": v(-11.05, 18.75) * mm});
            skLineSegment(sketch, "E291", {"start": v(-11.05, 18.75) * mm, "end": v(-10.97, 19.27) * mm});
            skLineSegment(sketch, "E292", {"start": v(-10.97, 19.27) * mm, "end": v(-10.86, 19.77) * mm});
            skLineSegment(sketch, "E293", {"start": v(-10.86, 19.77) * mm, "end": v(-10.73, 20.27) * mm});
            skLineSegment(sketch, "E294", {"start": v(-10.73, 20.27) * mm, "end": v(-10.58, 20.76) * mm});
            skLineSegment(sketch, "E295", {"start": v(-10.58, 20.76) * mm, "end": v(-10.4, 21.23) * mm});
            skLineSegment(sketch, "E296", {"start": v(-10.4, 21.23) * mm, "end": v(-10.2, 21.7) * mm});
            skLineSegment(sketch, "E297", {"start": v(-10.2, 21.7) * mm, "end": v(-10, 22.15) * mm});
            skLineSegment(sketch, "E298", {"start": v(-10, 22.15) * mm, "end": v(-9.76, 22.59) * mm});
            skLineSegment(sketch, "E299", {"start": v(-9.76, 22.59) * mm, "end": v(-9.5, 23.01) * mm});
            skLineSegment(sketch, "E300", {"start": v(-9.5, 23.01) * mm, "end": v(-9.24, 23.42) * mm});
            skLineSegment(sketch, "E301", {"start": v(-9.24, 23.42) * mm, "end": v(-8.95, 23.82) * mm});
            skLineSegment(sketch, "E302", {"start": v(-8.95, 23.82) * mm, "end": v(-8.64, 24.2) * mm});
            skLineSegment(sketch, "E303", {"start": v(-8.64, 24.2) * mm, "end": v(-8.32, 24.56) * mm});
            skLineSegment(sketch, "E304", {"start": v(-8.32, 24.56) * mm, "end": v(-7.98, 24.9) * mm});
            skLineSegment(sketch, "E305", {"start": v(-7.98, 24.9) * mm, "end": v(-7.63, 25.24) * mm});
            skLineSegment(sketch, "E306", {"start": v(-7.63, 25.24) * mm, "end": v(-7.26, 25.55) * mm});
            skLineSegment(sketch, "E307", {"start": v(-7.26, 25.55) * mm, "end": v(-6.88, 25.84) * mm});
            skLineSegment(sketch, "E308", {"start": v(-6.88, 25.84) * mm, "end": v(-6.49, 26.11) * mm});
            skLineSegment(sketch, "E309", {"start": v(-6.49, 26.11) * mm, "end": v(-6.08, 26.36) * mm});
            skLineSegment(sketch, "E310", {"start": v(-6.08, 26.36) * mm, "end": v(-5.66, 26.6) * mm});
            skLineSegment(sketch, "E311", {"start": v(-5.66, 26.6) * mm, "end": v(-5.23, 26.8) * mm});
            skLineSegment(sketch, "E312", {"start": v(-5.23, 26.8) * mm, "end": v(-4.8, 27) * mm});
            skLineSegment(sketch, "E313", {"start": v(-4.8, 27) * mm, "end": v(-4.34, 27.16) * mm});
            skLineSegment(sketch, "E314", {"start": v(-4.34, 27.16) * mm, "end": v(-3.88, 27.3) * mm});
            skLineSegment(sketch, "E315", {"start": v(-3.88, 27.3) * mm, "end": v(-3.4, 27.42) * mm});
            skLineSegment(sketch, "E316", {"start": v(-3.4, 27.42) * mm, "end": v(-2.93, 27.5) * mm});
            skLineSegment(sketch, "E317", {"start": v(-2.93, 27.5) * mm, "end": v(-2.44, 27.57) * mm});
            skLineSegment(sketch, "E318", {"start": v(-2.44, 27.57) * mm, "end": v(-1.95, 27.62) * mm});
            skLineSegment(sketch, "E319", {"start": v(-1.95, 27.62) * mm, "end": v(-1.45, 27.63) * mm});
            skLineSegment(sketch, "E320", {"start": v(-1.45, 27.63) * mm, "end": v(-0.95, 27.62) * mm});
            skLineSegment(sketch, "E321", {"start": v(-0.95, 27.62) * mm, "end": v(-0.46, 27.57) * mm});
            skLineSegment(sketch, "E322", {"start": v(-0.46, 27.57) * mm, "end": v(0.03, 27.5) * mm});
            skLineSegment(sketch, "E323", {"start": v(0.03, 27.5) * mm, "end": v(0.5, 27.42) * mm});
            skLineSegment(sketch, "E324", {"start": v(0.5, 27.42) * mm, "end": v(0.98, 27.3) * mm});
            skLineSegment(sketch, "E325", {"start": v(0.98, 27.3) * mm, "end": v(1.44, 27.16) * mm});
            skLineSegment(sketch, "E326", {"start": v(1.44, 27.16) * mm, "end": v(1.89, 27) * mm});
            skLineSegment(sketch, "E327", {"start": v(1.89, 27) * mm, "end": v(2.33, 26.8) * mm});
            skLineSegment(sketch, "E328", {"start": v(2.33, 26.8) * mm, "end": v(2.76, 26.6) * mm});
            skLineSegment(sketch, "E329", {"start": v(2.76, 26.6) * mm, "end": v(3.18, 26.36) * mm});
            skLineSegment(sketch, "E330", {"start": v(3.18, 26.36) * mm, "end": v(3.59, 26.11) * mm});
            skLineSegment(sketch, "E331", {"start": v(3.59, 26.11) * mm, "end": v(3.98, 25.84) * mm});
            skLineSegment(sketch, "E332", {"start": v(3.98, 25.84) * mm, "end": v(4.36, 25.55) * mm});
            skLineSegment(sketch, "E333", {"start": v(4.36, 25.55) * mm, "end": v(4.73, 25.24) * mm});
            skLineSegment(sketch, "E334", {"start": v(4.73, 25.24) * mm, "end": v(5.08, 24.9) * mm});
            skLineSegment(sketch, "E335", {"start": v(5.08, 24.9) * mm, "end": v(5.42, 24.56) * mm});
            skLineSegment(sketch, "E336", {"start": v(5.42, 24.56) * mm, "end": v(5.74, 24.2) * mm});
            skLineSegment(sketch, "E337", {"start": v(5.74, 24.2) * mm, "end": v(6.05, 23.82) * mm});
            skLineSegment(sketch, "E338", {"start": v(6.05, 23.82) * mm, "end": v(6.33, 23.42) * mm});
            skLineSegment(sketch, "E339", {"start": v(6.33, 23.42) * mm, "end": v(6.6, 23.01) * mm});
            skLineSegment(sketch, "E340", {"start": v(6.6, 23.01) * mm, "end": v(6.86, 22.59) * mm});
            skLineSegment(sketch, "E341", {"start": v(6.86, 22.59) * mm, "end": v(7.1, 22.15) * mm});
            skLineSegment(sketch, "E342", {"start": v(7.1, 22.15) * mm, "end": v(7.3, 21.7) * mm});
            skLineSegment(sketch, "E343", {"start": v(7.3, 21.7) * mm, "end": v(7.5, 21.23) * mm});
            skLineSegment(sketch, "E344", {"start": v(7.5, 21.23) * mm, "end": v(7.67, 20.76) * mm});
            skLineSegment(sketch, "E345", {"start": v(7.67, 20.76) * mm, "end": v(7.83, 20.27) * mm});
            skLineSegment(sketch, "E346", {"start": v(7.83, 20.27) * mm, "end": v(7.96, 19.77) * mm});
            skLineSegment(sketch, "E347", {"start": v(7.96, 19.77) * mm, "end": v(8.07, 19.27) * mm});
            skLineSegment(sketch, "E348", {"start": v(8.07, 19.27) * mm, "end": v(8.15, 18.75) * mm});
            skLineSegment(sketch, "E349", {"start": v(8.15, 18.75) * mm, "end": v(8.21, 18.23) * mm});
            skLineSegment(sketch, "E350", {"start": v(8.21, 18.23) * mm, "end": v(8.25, 17.7) * mm});
            skLineSegment(sketch, "E351", {"start": v(8.25, 17.7) * mm, "end": v(8.26, 17.16) * mm});
            skLineSegment(sketch, "E352", {"start": v(8.26, 17.16) * mm, "end": v(8.25, 16.62) * mm});
            skLineSegment(sketch, "E353", {"start": v(8.25, 16.62) * mm, "end": v(8.21, 16.09) * mm});
            skLineSegment(sketch, "E354", {"start": v(8.21, 16.09) * mm, "end": v(8.15, 15.56) * mm});
            skLineSegment(sketch, "E355", {"start": v(8.15, 15.56) * mm, "end": v(8.07, 15.05) * mm});
            skLineSegment(sketch, "E356", {"start": v(8.07, 15.05) * mm, "end": v(7.96, 14.54) * mm});
            skLineSegment(sketch, "E357", {"start": v(7.96, 14.54) * mm, "end": v(7.83, 14.04) * mm});
            skLineSegment(sketch, "E358", {"start": v(7.83, 14.04) * mm, "end": v(7.67, 13.56) * mm});
            skLineSegment(sketch, "E359", {"start": v(7.67, 13.56) * mm, "end": v(7.5, 13.08) * mm});
            skLineSegment(sketch, "E360", {"start": v(7.5, 13.08) * mm, "end": v(7.3, 12.62) * mm});
            skLineSegment(sketch, "E361", {"start": v(7.3, 12.62) * mm, "end": v(7.1, 12.17) * mm});
            skLineSegment(sketch, "E362", {"start": v(7.1, 12.17) * mm, "end": v(6.86, 11.73) * mm});
            skLineSegment(sketch, "E363", {"start": v(6.86, 11.73) * mm, "end": v(6.6, 11.3) * mm});
            skLineSegment(sketch, "E364", {"start": v(6.6, 11.3) * mm, "end": v(6.33, 10.9) * mm});
            skLineSegment(sketch, "E365", {"start": v(6.33, 10.9) * mm, "end": v(6.05, 10.5) * mm});
            skLineSegment(sketch, "E366", {"start": v(6.05, 10.5) * mm, "end": v(5.74, 10.12) * mm});
            skLineSegment(sketch, "E367", {"start": v(5.74, 10.12) * mm, "end": v(5.42, 9.75) * mm});
            skLineSegment(sketch, "E368", {"start": v(5.42, 9.75) * mm, "end": v(5.08, 9.4) * mm});
            skLineSegment(sketch, "E369", {"start": v(5.08, 9.4) * mm, "end": v(4.73, 9.08) * mm});
            skLineSegment(sketch, "E370", {"start": v(4.73, 9.08) * mm, "end": v(4.36, 8.77) * mm});
            skLineSegment(sketch, "E371", {"start": v(4.36, 8.77) * mm, "end": v(3.98, 8.47) * mm});
            skLineSegment(sketch, "E372", {"start": v(3.98, 8.47) * mm, "end": v(3.59, 8.2) * mm});
            skLineSegment(sketch, "E373", {"start": v(3.59, 8.2) * mm, "end": v(3.18, 7.95) * mm});
            skLineSegment(sketch, "E374", {"start": v(3.18, 7.95) * mm, "end": v(2.76, 7.72) * mm});
            skLineSegment(sketch, "E375", {"start": v(2.76, 7.72) * mm, "end": v(2.33, 7.5) * mm});
            skLineSegment(sketch, "E376", {"start": v(2.33, 7.5) * mm, "end": v(1.89, 7.32) * mm});
            skLineSegment(sketch, "E377", {"start": v(1.89, 7.32) * mm, "end": v(1.44, 7.16) * mm});
            skLineSegment(sketch, "E378", {"start": v(1.44, 7.16) * mm, "end": v(0.98, 7.02) * mm});
            skLineSegment(sketch, "E379", {"start": v(0.98, 7.02) * mm, "end": v(0.5, 6.9) * mm});
            skLineSegment(sketch, "E380", {"start": v(0.5, 6.9) * mm, "end": v(0.03, 6.8) * mm});
            skLineSegment(sketch, "E381", {"start": v(0.03, 6.8) * mm, "end": v(-0.46, 6.74) * mm});
            skLineSegment(sketch, "E382", {"start": v(-0.46, 6.74) * mm, "end": v(-0.95, 6.7) * mm});
            skLineSegment(sketch, "E383", {"start": v(-0.95, 6.7) * mm, "end": v(-1.45, 6.69) * mm});
            skLineSegment(sketch, "E384", {"start": v(-1.45, 6.69) * mm, "end": v(-1.5, 6.69) * mm});
            skLineSegment(sketch, "E385", {"start": v(-1.5, 6.69) * mm, "end": v(-1.56, 6.69) * mm});
            skLineSegment(sketch, "E386", {"start": v(-1.56, 6.69) * mm, "end": v(-1.65, 6.69) * mm});
            skLineSegment(sketch, "E387", {"start": v(-1.65, 6.69) * mm, "end": v(-1.75, 6.69) * mm});
            skLineSegment(sketch, "E388", {"start": v(-1.75, 6.69) * mm, "end": v(-1.87, 6.69) * mm});
            skLineSegment(sketch, "E389", {"start": v(-1.87, 6.69) * mm, "end": v(-2, 6.69) * mm});
            skLineSegment(sketch, "E390", {"start": v(-2, 6.69) * mm, "end": v(-2.15, 6.69) * mm});
            skLineSegment(sketch, "E391", {"start": v(-2.15, 6.69) * mm, "end": v(-2.3, 6.69) * mm});
            skLineSegment(sketch, "E392", {"start": v(-2.3, 6.69) * mm, "end": v(-2.47, 6.69) * mm});
            skLineSegment(sketch, "E393", {"start": v(-2.47, 6.69) * mm, "end": v(-2.65, 6.69) * mm});
            skLineSegment(sketch, "E394", {"start": v(-2.65, 6.69) * mm, "end": v(-2.83, 6.69) * mm});
            skLineSegment(sketch, "E395", {"start": v(-2.83, 6.69) * mm, "end": v(-3.02, 6.69) * mm});
            skLineSegment(sketch, "E396", {"start": v(-3.02, 6.69) * mm, "end": v(-3.22, 6.69) * mm});
            skLineSegment(sketch, "E397", {"start": v(-3.22, 6.69) * mm, "end": v(-3.42, 6.69) * mm});
            skLineSegment(sketch, "E398", {"start": v(-3.42, 6.69) * mm, "end": v(-3.62, 6.69) * mm});
            skLineSegment(sketch, "E399", {"start": v(-3.62, 6.69) * mm, "end": v(-3.82, 6.69) * mm});
            skLineSegment(sketch, "E400", {"start": v(-3.82, 6.69) * mm, "end": v(-4.02, 6.69) * mm});
            skLineSegment(sketch, "E401", {"start": v(-4.02, 6.69) * mm, "end": v(-4.21, 6.69) * mm});
            skLineSegment(sketch, "E402", {"start": v(-4.21, 6.69) * mm, "end": v(-4.4, 6.69) * mm});
            skLineSegment(sketch, "E403", {"start": v(-4.4, 6.69) * mm, "end": v(-4.6, 6.69) * mm});
            skLineSegment(sketch, "E404", {"start": v(-4.6, 6.69) * mm, "end": v(-4.78, 6.69) * mm});
            skLineSegment(sketch, "E405", {"start": v(-4.78, 6.69) * mm, "end": v(-4.95, 6.69) * mm});
            skLineSegment(sketch, "E406", {"start": v(-4.95, 6.69) * mm, "end": v(-5.11, 6.69) * mm});
            skLineSegment(sketch, "E407", {"start": v(-5.11, 6.69) * mm, "end": v(-5.26, 6.69) * mm});
            skLineSegment(sketch, "E408", {"start": v(-5.26, 6.69) * mm, "end": v(-5.4, 6.69) * mm});
            skLineSegment(sketch, "E409", {"start": v(-5.4, 6.69) * mm, "end": v(-5.53, 6.69) * mm});
            skLineSegment(sketch, "E410", {"start": v(-5.53, 6.69) * mm, "end": v(-5.64, 6.69) * mm});
            skLineSegment(sketch, "E411", {"start": v(-5.64, 6.69) * mm, "end": v(-5.73, 6.69) * mm});
            skLineSegment(sketch, "E412", {"start": v(-5.73, 6.69) * mm, "end": v(-5.8, 6.69) * mm});
            skLineSegment(sketch, "E413", {"start": v(-5.8, 6.69) * mm, "end": v(-5.86, 6.69) * mm});
            skLineSegment(sketch, "E414", {"start": v(-5.86, 6.69) * mm, "end": v(-5.9, 6.69) * mm});
            skLineSegment(sketch, "E415", {"start": v(-5.9, 6.69) * mm, "end": v(-5.9, 6.69) * mm});
            skLineSegment(sketch, "E416", {"start": v(-5.9, 6.69) * mm, "end": v(-5.9, 6.36) * mm});
            skLineSegment(sketch, "E417", {"start": v(-5.9, 6.36) * mm, "end": v(-5.9, 6.03) * mm});
            skLineSegment(sketch, "E418", {"start": v(-5.9, 6.03) * mm, "end": v(-5.9, 5.7) * mm});
            skLineSegment(sketch, "E419", {"start": v(-5.9, 5.7) * mm, "end": v(-5.9, 5.37) * mm});
            skLineSegment(sketch, "E420", {"start": v(-5.9, 5.37) * mm, "end": v(-5.9, 5.05) * mm});
            skLineSegment(sketch, "E421", {"start": v(-5.9, 5.05) * mm, "end": v(-5.9, 4.72) * mm});
            skLineSegment(sketch, "E422", {"start": v(-5.9, 4.72) * mm, "end": v(-5.9, 4.39) * mm});
            skLineSegment(sketch, "E423", {"start": v(-5.9, 4.39) * mm, "end": v(-5.9, 4.06) * mm});
            skLineSegment(sketch, "E424", {"start": v(-5.9, 4.06) * mm, "end": v(-5.9, 3.73) * mm});
            skLineSegment(sketch, "E425", {"start": v(-5.9, 3.73) * mm, "end": v(-5.9, 3.4) * mm});
            skLineSegment(sketch, "E426", {"start": v(-5.9, 3.4) * mm, "end": v(-5.9, 3.08) * mm});
            skLineSegment(sketch, "E427", {"start": v(-5.9, 3.08) * mm, "end": v(-5.9, 2.75) * mm});
            skLineSegment(sketch, "E428", {"start": v(-5.9, 2.75) * mm, "end": v(-5.9, 2.42) * mm});
            skLineSegment(sketch, "E429", {"start": v(-5.9, 2.42) * mm, "end": v(-5.9, 2.1) * mm});
            skLineSegment(sketch, "E430", {"start": v(-5.9, 2.1) * mm, "end": v(-5.9, 1.76) * mm});
            skLineSegment(sketch, "E431", {"start": v(-5.9, 1.76) * mm, "end": v(-5.9, 1.44) * mm});
            skLineSegment(sketch, "E432", {"start": v(-5.9, 1.44) * mm, "end": v(-5.9, 1.1) * mm});
            skLineSegment(sketch, "E433", {"start": v(-5.9, 1.1) * mm, "end": v(-5.9, 0.78) * mm});
            skLineSegment(sketch, "E434", {"start": v(-5.9, 0.78) * mm, "end": v(-5.9, 0.45) * mm});
            skLineSegment(sketch, "E435", {"start": v(-5.9, 0.45) * mm, "end": v(-5.9, 0.12) * mm});
            skLineSegment(sketch, "E436", {"start": v(-5.9, 0.12) * mm, "end": v(-5.9, -0.2) * mm});
            skLineSegment(sketch, "E437", {"start": v(-5.9, -0.2) * mm, "end": v(-5.9, -0.53) * mm});
            skLineSegment(sketch, "E438", {"start": v(-5.9, -0.53) * mm, "end": v(-5.9, -0.86) * mm});
            skLineSegment(sketch, "E439", {"start": v(-5.9, -0.86) * mm, "end": v(-5.9, -1.2) * mm});
            skLineSegment(sketch, "E440", {"start": v(-5.9, -1.2) * mm, "end": v(-5.9, -1.52) * mm});
            skLineSegment(sketch, "E441", {"start": v(-5.9, -1.52) * mm, "end": v(-5.9, -1.85) * mm});
            skLineSegment(sketch, "E442", {"start": v(-5.9, -1.85) * mm, "end": v(-5.9, -2.18) * mm});
            skLineSegment(sketch, "E443", {"start": v(-5.9, -2.18) * mm, "end": v(-5.9, -2.5) * mm});
            skLineSegment(sketch, "E444", {"start": v(-5.9, -2.5) * mm, "end": v(-5.9, -2.83) * mm});
            skLineSegment(sketch, "E445", {"start": v(-5.9, -2.83) * mm, "end": v(-5.9, -3.16) * mm});
            skLineSegment(sketch, "E446", {"start": v(-5.9, -3.16) * mm, "end": v(-5.9, -3.49) * mm});
            skLineSegment(sketch, "E447", {"start": v(-5.9, -3.49) * mm, "end": v(-5.9, -3.82) * mm});
            skLineSegment(sketch, "E448", {"start": v(-5.9, -3.82) * mm, "end": v(-5.9, -3.82) * mm});
            skLineSegment(sketch, "E449", {"start": v(-5.9, -3.82) * mm, "end": v(-5.85, -3.82) * mm});
            skLineSegment(sketch, "E450", {"start": v(-5.85, -3.82) * mm, "end": v(-5.78, -3.82) * mm});
            skLineSegment(sketch, "E451", {"start": v(-5.78, -3.82) * mm, "end": v(-5.7, -3.82) * mm});
            skLineSegment(sketch, "E452", {"start": v(-5.7, -3.82) * mm, "end": v(-5.57, -3.82) * mm});
            skLineSegment(sketch, "E453", {"start": v(-5.57, -3.82) * mm, "end": v(-5.44, -3.82) * mm});
            skLineSegment(sketch, "E454", {"start": v(-5.44, -3.82) * mm, "end": v(-5.28, -3.82) * mm});
            skLineSegment(sketch, "E455", {"start": v(-5.28, -3.82) * mm, "end": v(-5.1, -3.82) * mm});
            skLineSegment(sketch, "E456", {"start": v(-5.1, -3.82) * mm, "end": v(-4.92, -3.82) * mm});
            skLineSegment(sketch, "E457", {"start": v(-4.92, -3.82) * mm, "end": v(-4.71, -3.82) * mm});
            skLineSegment(sketch, "E458", {"start": v(-4.71, -3.82) * mm, "end": v(-4.5, -3.82) * mm});
            skLineSegment(sketch, "E459", {"start": v(-4.5, -3.82) * mm, "end": v(-4.27, -3.82) * mm});
            skLineSegment(sketch, "E460", {"start": v(-4.27, -3.82) * mm, "end": v(-4.03, -3.82) * mm});
            skLineSegment(sketch, "E461", {"start": v(-4.03, -3.82) * mm, "end": v(-3.79, -3.82) * mm});
            skLineSegment(sketch, "E462", {"start": v(-3.79, -3.82) * mm, "end": v(-3.54, -3.82) * mm});
            skLineSegment(sketch, "E463", {"start": v(-3.54, -3.82) * mm, "end": v(-3.28, -3.82) * mm});
            skLineSegment(sketch, "E464", {"start": v(-3.28, -3.82) * mm, "end": v(-3.03, -3.82) * mm});
            skLineSegment(sketch, "E465", {"start": v(-3.03, -3.82) * mm, "end": v(-2.77, -3.82) * mm});
            skLineSegment(sketch, "E466", {"start": v(-2.77, -3.82) * mm, "end": v(-2.5, -3.82) * mm});
            skLineSegment(sketch, "E467", {"start": v(-2.5, -3.82) * mm, "end": v(-2.25, -3.82) * mm});
            skLineSegment(sketch, "E468", {"start": v(-2.25, -3.82) * mm, "end": v(-2, -3.82) * mm});
            skLineSegment(sketch, "E469", {"start": v(-2, -3.82) * mm, "end": v(-1.76, -3.82) * mm});
            skLineSegment(sketch, "E470", {"start": v(-1.76, -3.82) * mm, "end": v(-1.52, -3.82) * mm});
            skLineSegment(sketch, "E471", {"start": v(-1.52, -3.82) * mm, "end": v(-1.3, -3.82) * mm});
            skLineSegment(sketch, "E472", {"start": v(-1.3, -3.82) * mm, "end": v(-1.08, -3.82) * mm});
            skLineSegment(sketch, "E473", {"start": v(-1.08, -3.82) * mm, "end": v(-0.87, -3.82) * mm});
            skLineSegment(sketch, "E474", {"start": v(-0.87, -3.82) * mm, "end": v(-0.68, -3.82) * mm});
            skLineSegment(sketch, "E475", {"start": v(-0.68, -3.82) * mm, "end": v(-0.5, -3.82) * mm});
            skLineSegment(sketch, "E476", {"start": v(-0.5, -3.82) * mm, "end": v(-0.35, -3.82) * mm});
            skLineSegment(sketch, "E477", {"start": v(-0.35, -3.82) * mm, "end": v(-0.21, -3.82) * mm});
            skLineSegment(sketch, "E478", {"start": v(-0.21, -3.82) * mm, "end": v(-0.1, -3.82) * mm});
            skLineSegment(sketch, "E479", {"start": v(-0.1, -3.82) * mm, "end": v(0, -3.82) * mm});
            skLineSegment(sketch, "E480", {"start": v(0, -3.82) * mm, "end": v(0.57, -3.83) * mm});
            skLineSegment(sketch, "E481", {"start": v(0.57, -3.83) * mm, "end": v(1.14, -3.88) * mm});
            skLineSegment(sketch, "E482", {"start": v(1.14, -3.88) * mm, "end": v(1.7, -3.95) * mm});
            skLineSegment(sketch, "E483", {"start": v(1.7, -3.95) * mm, "end": v(2.25, -4.06) * mm});
            skLineSegment(sketch, "E484", {"start": v(2.25, -4.06) * mm, "end": v(2.8, -4.2) * mm});
            skLineSegment(sketch, "E485", {"start": v(2.8, -4.2) * mm, "end": v(3.32, -4.35) * mm});
            skLineSegment(sketch, "E486", {"start": v(3.32, -4.35) * mm, "end": v(3.84, -4.54) * mm});
            skLineSegment(sketch, "E487", {"start": v(3.84, -4.54) * mm, "end": v(4.35, -4.75) * mm});
            skLineSegment(sketch, "E488", {"start": v(4.35, -4.75) * mm, "end": v(4.84, -4.99) * mm});
            skLineSegment(sketch, "E489", {"start": v(4.84, -4.99) * mm, "end": v(5.32, -5.25) * mm});
            skLineSegment(sketch, "E490", {"start": v(5.32, -5.25) * mm, "end": v(5.79, -5.54) * mm});
            skLineSegment(sketch, "E491", {"start": v(5.79, -5.54) * mm, "end": v(6.24, -5.85) * mm});
            skLineSegment(sketch, "E492", {"start": v(6.24, -5.85) * mm, "end": v(6.68, -6.18) * mm});
            skLineSegment(sketch, "E493", {"start": v(6.68, -6.18) * mm, "end": v(7.1, -6.53) * mm});
            skLineSegment(sketch, "E494", {"start": v(7.1, -6.53) * mm, "end": v(7.5, -6.9) * mm});
            skLineSegment(sketch, "E495", {"start": v(7.5, -6.9) * mm, "end": v(7.9, -7.3) * mm});
            skLineSegment(sketch, "E496", {"start": v(7.9, -7.3) * mm, "end": v(8.26, -7.71) * mm});
            skLineSegment(sketch, "E497", {"start": v(8.26, -7.71) * mm, "end": v(8.62, -8.14) * mm});
            skLineSegment(sketch, "E498", {"start": v(8.62, -8.14) * mm, "end": v(8.95, -8.6) * mm});
            skLineSegment(sketch, "E499", {"start": v(8.95, -8.6) * mm, "end": v(9.26, -9.06) * mm});
            skLineSegment(sketch, "E500", {"start": v(9.26, -9.06) * mm, "end": v(9.55, -9.54) * mm});
            skLineSegment(sketch, "E501", {"start": v(9.55, -9.54) * mm, "end": v(9.82, -10.04) * mm});
            skLineSegment(sketch, "E502", {"start": v(9.82, -10.04) * mm, "end": v(10.06, -10.55) * mm});
            skLineSegment(sketch, "E503", {"start": v(10.06, -10.55) * mm, "end": v(10.29, -11.08) * mm});
            skLineSegment(sketch, "E504", {"start": v(10.29, -11.08) * mm, "end": v(10.49, -11.62) * mm});
            skLineSegment(sketch, "E505", {"start": v(10.49, -11.62) * mm, "end": v(10.66, -12.17) * mm});
            skLineSegment(sketch, "E506", {"start": v(10.66, -12.17) * mm, "end": v(10.81, -12.74) * mm});
            skLineSegment(sketch, "E507", {"start": v(10.81, -12.74) * mm, "end": v(10.94, -13.31) * mm});
            skLineSegment(sketch, "E508", {"start": v(10.94, -13.31) * mm, "end": v(11.04, -13.9) * mm});
            skLineSegment(sketch, "E509", {"start": v(11.04, -13.9) * mm, "end": v(11.1, -14.5) * mm});
            skLineSegment(sketch, "E510", {"start": v(11.1, -14.5) * mm, "end": v(11.15, -15.1) * mm});
            skLineSegment(sketch, "E511", {"start": v(11.15, -15.1) * mm, "end": v(11.17, -15.7) * mm});
            skLineSegment(sketch, "E512", {"start": v(11.17, -15.7) * mm, "end": v(11.15, -16.32) * mm});
            skLineSegment(sketch, "E513", {"start": v(11.15, -16.32) * mm, "end": v(11.1, -16.92) * mm});
            skLineSegment(sketch, "E514", {"start": v(11.1, -16.92) * mm, "end": v(11.04, -17.52) * mm});
            skLineSegment(sketch, "E515", {"start": v(11.04, -17.52) * mm, "end": v(10.94, -18.1) * mm});
            skLineSegment(sketch, "E516", {"start": v(10.94, -18.1) * mm, "end": v(10.81, -18.68) * mm});
            skLineSegment(sketch, "E517", {"start": v(10.81, -18.68) * mm, "end": v(10.66, -19.24) * mm});
            skLineSegment(sketch, "E518", {"start": v(10.66, -19.24) * mm, "end": v(10.49, -19.8) * mm});
            skLineSegment(sketch, "E519", {"start": v(10.49, -19.8) * mm, "end": v(10.29, -20.34) * mm});
            skLineSegment(sketch, "E520", {"start": v(10.29, -20.34) * mm, "end": v(10.06, -20.86) * mm});
            skLineSegment(sketch, "E521", {"start": v(10.06, -20.86) * mm, "end": v(9.82, -21.37) * mm});
            skLineSegment(sketch, "E522", {"start": v(9.82, -21.37) * mm, "end": v(9.55, -21.87) * mm});
            skLineSegment(sketch, "E523", {"start": v(9.55, -21.87) * mm, "end": v(9.26, -22.35) * mm});
            skLineSegment(sketch, "E524", {"start": v(9.26, -22.35) * mm, "end": v(8.95, -22.82) * mm});
            skLineSegment(sketch, "E525", {"start": v(8.95, -22.82) * mm, "end": v(8.62, -23.27) * mm});
            skLineSegment(sketch, "E526", {"start": v(8.62, -23.27) * mm, "end": v(8.26, -23.7) * mm});
            skLineSegment(sketch, "E527", {"start": v(8.26, -23.7) * mm, "end": v(7.9, -24.11) * mm});
            skLineSegment(sketch, "E528", {"start": v(7.9, -24.11) * mm, "end": v(7.5, -24.5) * mm});
            skLineSegment(sketch, "E529", {"start": v(7.5, -24.5) * mm, "end": v(7.1, -24.88) * mm});
            skLineSegment(sketch, "E530", {"start": v(7.1, -24.88) * mm, "end": v(6.68, -25.24) * mm});
            skLineSegment(sketch, "E531", {"start": v(6.68, -25.24) * mm, "end": v(6.24, -25.57) * mm});
            skLineSegment(sketch, "E532", {"start": v(6.24, -25.57) * mm, "end": v(5.79, -25.88) * mm});
            skLineSegment(sketch, "E533", {"start": v(5.79, -25.88) * mm, "end": v(5.32, -26.16) * mm});
            skLineSegment(sketch, "E534", {"start": v(5.32, -26.16) * mm, "end": v(4.84, -26.42) * mm});
            skLineSegment(sketch, "E535", {"start": v(4.84, -26.42) * mm, "end": v(4.35, -26.66) * mm});
            skLineSegment(sketch, "E536", {"start": v(4.35, -26.66) * mm, "end": v(3.84, -26.88) * mm});
            skLineSegment(sketch, "E537", {"start": v(3.84, -26.88) * mm, "end": v(3.32, -27.06) * mm});
            skLineSegment(sketch, "E538", {"start": v(3.32, -27.06) * mm, "end": v(2.8, -27.22) * mm});
            skLineSegment(sketch, "E539", {"start": v(2.8, -27.22) * mm, "end": v(2.25, -27.36) * mm});
            skLineSegment(sketch, "E540", {"start": v(2.25, -27.36) * mm, "end": v(1.7, -27.46) * mm});
            skLineSegment(sketch, "E541", {"start": v(1.7, -27.46) * mm, "end": v(1.14, -27.54) * mm});
            skLineSegment(sketch, "E542", {"start": v(1.14, -27.54) * mm, "end": v(0.57, -27.58) * mm});
            skLineSegment(sketch, "E543", {"start": v(0.57, -27.58) * mm, "end": v(0, -27.6) * mm});
            skSolve(sketch);
        }
        {
            var Q0;
            Q0 = qSketchRegion(id + "F0", true);
            extrude(context, id + "F1", {"entities" : qUnion([Q0]), "depth" : 12.7 * mm, "offsetDistance" : 25.4 * mm});
        }
    });
